# Revit family: HDX Series Conference System_rev0_2022
name_source: partatom
category: Communication Devices
units: mm (PartAtom-declared; Revit-internal decimal feet)

## family parameters
Cut with Voids When Loaded = No
Host = Face
Maintain Annotation Orientation = No
Part Type = Normal
Room Calculation Point = No
Round Connector Dimension = Use Diameter
Shared = Yes

## types (4) — shared parameters
Default Elevation = 4' - 0"
Manufacturer = Nereva

## per-type parameters (varying)
| type | Accessories (Included) | Audio Bar | Case Depth | Case Finish | Case Height | Case Width | Communication Formats | Communication Ports | Connections | Frequency Range | Grille | HUB | Hardware | LF Enclousre | Loudspeaker Power | Microphones | POD | Scrim | Sensitivity | Speakers | URL | Weight Dimensional |
| HDX-BAR-B | Mounting Bracket, Documentation | Yes | 0' - 3 15/16" | Laminate, Black | 3' - 0" | 0' - 10 3/4" |  |  | RJ45 — for connection to system hub | 120 Hz to 20 kHz | Black Grille | No | Steel - Black Powder coated | Vented speaker enclosure for enhanced low-frequency response | Built-in amplifier and crossover | 10 low-noise omnidirectional MEMS, Frequency response of 100 Hz to 10 kHz | No | Plastic, Opaque Black | 92 | 2 x 4" neodymium driver - 30 W RMS and 60 W max
1 x 1" teteron dome tweeter - 10 W RMS and 20 W max | https://www.nureva.com | 22.5 |
| HDX-POD | Mounting Bracket, T-bar Clip, Documentation | No | 0' - 2 3/8" | Laminate, Black | 1' - 4" | 0' - 6 1/2" |  |  | RJ45 — for connection to system hub |  | White Grille | No | Steel - Black Powder coated |  |  | 10 low-noise omnidirectional MEMS, Frequency response of 100 Hz to 10 kHz | Yes | Grille Scrim - White | 0 |  | https://www.nureva.com | 0 |
| HDX-HUB | Mounting bracket, Country-specific power cable, USB Type-C cable, USB-C to USB-A adapter, Remote with Bluetooth technology, Documentation | No | 0' - 6" | Laminate, Black | 0' - 5 27/32" | 1' - 0 5/32" | LAN and Dante 2x2 AVoIP, RJ45, Bluetooth® LE technology radio antenna USB 2.0 interface to computer, Integrated Auracast transmitter  
or collaboration hub, Type-C | 6 connections to audio bars and microphone pods, RJ45 | Input jack for power supply, 4 analog audio input channels,  
balanced, Euroblock 3.5 mm pitch, 2 analog audio output channels, 
balanced, Euroblock 3.5 mm pitch, Subwoofer connection, balanced, ¼" jack |  | White Grille | Yes | Steel - Black Powder coated |  |  |  | No | Grille Scrim - White | 0 |  |  | 0 |
| HDX-BAR-W | Mounting Bracket, Documentation | Yes | 0' - 3 15/16" | Laminate, White, Matte | 3' - 0" | 0' - 10 3/4" |  |  | RJ45 — for connection to system hub | 120 Hz to 20 kHz | White Grille | No | Metal, Paint Finish, White, Matte | Vented speaker enclosure for enhanced low-frequency response | Built-in amplifier and crossover | 10 low-noise omnidirectional MEMS, Frequency response of 100 Hz to 10 kHz | No | Grille Scrim - White | 92 | 2 x 4" neodymium driver - 30 W RMS and 60 W max
1 x 1" teteron dome tweeter - 10 W RMS and 20 W max | https://www.nureva.com | 22.5 |

note: column(s) folded — value = type name in every type: Model, Part Number

## geometry (parser evidence)
native form markers: Sweep x9
no freeform markers — native parametric forms only
